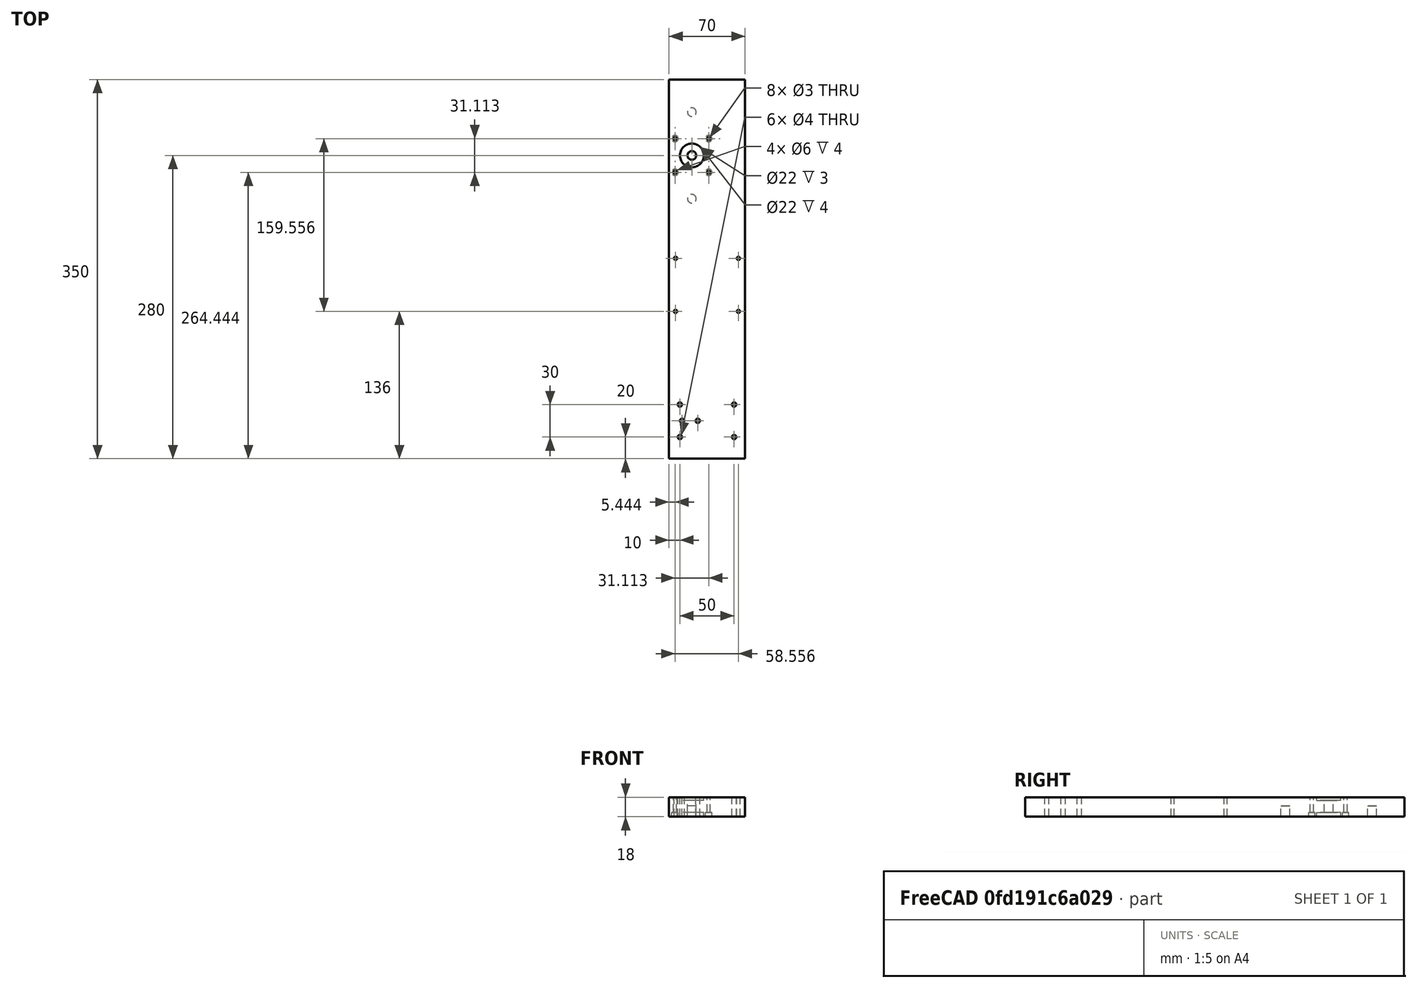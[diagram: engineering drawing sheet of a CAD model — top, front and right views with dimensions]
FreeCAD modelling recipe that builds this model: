
FCSTD DOCUMENT  (FreeCAD 0.17R13541 (Git))
Label: X-Izquierda
License: All rights reserved
LicenseURL: http://en.wikipedia.org/wiki/All_rights_reserved
objects: Part::Cylinder×16, Part::Cut×6, Part::MultiFuse×3, Part::FeaturePython×3, Part::Box×1
note: 29 computed .brp shape members not serialized (recipe doc carries the construction recipe); baked Part::Feature solids carry a one-line shape summary decoded from their .brp

FEATURE [Part::Box] Box  label="Base"
  AttacherType = Attacher::AttachEngine3D
  Height = 18
  Length = 70
  Width = 350
FEATURE [Part::Cylinder] Cylinder  label="Cilindro"
  Angle = 360
  AttacherType = Attacher::AttachEngine3D
  Height = 25
  Placement = pos=(10,20,0) rot=(0,0,1;0rad)
  Radius = 2
FEATURE [Part::Cylinder] Cylinder001  label="Cilindro001"
  Angle = 360
  AttacherType = Attacher::AttachEngine3D
  Height = 25
  Placement = pos=(60,20,0) rot=(0,0,1;0rad)
  Radius = 2
FEATURE [Part::Cylinder] Cylinder002  label="Cilindro002"
  Angle = 360
  AttacherType = Attacher::AttachEngine3D
  Height = 25
  Placement = pos=(10,50,0) rot=(0,0,1;0rad)
  Radius = 2
FEATURE [Part::Cylinder] Cylinder003  label="Cilindro003"
  Angle = 360
  AttacherType = Attacher::AttachEngine3D
  Height = 25
  Placement = pos=(60,50,0) rot=(0,0,1;0rad)
  Radius = 2
FEATURE [Part::Cylinder] Cylinder004  label="Cilindro004"
  Angle = 360
  AttacherType = Attacher::AttachEngine3D
  Height = 25
  Placement = pos=(12,35,0) rot=(0,0,1;0rad)
  Radius = 2
FEATURE [Part::Cylinder] Cylinder005  label="Cilindro005"
  Angle = 360
  AttacherType = Attacher::AttachEngine3D
  Height = 25
  Placement = pos=(26.5,35,0) rot=(0,0,1;0rad)
  Radius = 2
FEATURE [Part::MultiFuse] Fusion
  Refine = true
  Shapes = -> [Cylinder005,Cylinder003,Cylinder004,Cylinder002,Cylinder001,Cylinder]
FEATURE [Part::Cylinder] Cylinder006  label="Cilindro006"
  Angle = 360
  AttacherType = Attacher::AttachEngine3D
  Height = 25
  Placement = pos=(64,136,0) rot=(0,0,1;0rad)
  Radius = 1.5
FEATURE [Part::Cylinder] Cylinder007  label="Cilindro007"
  Angle = 360
  AttacherType = Attacher::AttachEngine3D
  Height = 25
  Placement = pos=(6,136,0) rot=(0,0,1;0rad)
  Radius = 1.5
FEATURE [Part::Cylinder] Cylinder008  label="Cilindro008"
  Angle = 360
  AttacherType = Attacher::AttachEngine3D
  Height = 25
  Placement = pos=(6,185,0) rot=(0,0,1;0rad)
  Radius = 1.5
FEATURE [Part::Cylinder] Cylinder009  label="Cilindro009"
  Angle = 360
  AttacherType = Attacher::AttachEngine3D
  Height = 25
  Placement = pos=(64,185,0) rot=(0,0,1;0rad)
  Radius = 1.5
FEATURE [Part::Cut] Cut
  Base = -> Box
  Refine = true
  Tool = -> Fusion
FEATURE [Part::MultiFuse] Fusion001
  Refine = true
  Shapes = -> [Cylinder009,Cylinder008,Cylinder007,Cylinder006]
FEATURE [Part::Cut] Cut001
  Base = -> Cut
  Refine = true
  Tool = -> Fusion001
FEATURE [Part::Cylinder] Cylinder010  label="Cilindro010"
  Angle = 360
  AttacherType = Attacher::AttachEngine3D
  Height = 25
  Placement = pos=(22,0,0) rot=(0,0,1;0rad)
  Radius = 1.5
FEATURE [Part::FeaturePython] Array  # Draft array (typed FeaturePython)
  Angle = 360
  ArrayType = 1
  Axis = (0,0,1)
  Base = -> Cylinder010
  Center = (0,0,0)
  Fuse = false
  IntervalAxis = (0,0,0)
  IntervalX = (1,0,0)
  IntervalY = (0,1,0)
  IntervalZ = (0,0,0)
  NumberPolar = 4
  NumberX = 2
  NumberY = 2
  NumberZ = 1
  Placement = pos=(21,280,0) rot=(0,0,1;0.785398rad)
FEATURE [Part::Cylinder] Cylinder011  label="Cilindro011"
  Angle = 360
  AttacherType = Attacher::AttachEngine3D
  Height = 25
  Radius = 4
FEATURE [Part::Cylinder] Cylinder012  label="Cilindro012"
  Angle = 360
  AttacherType = Attacher::AttachEngine3D
  Height = 10
  Placement = pos=(0,0,15) rot=(0,0,1;0rad)
  Radius = 11
FEATURE [Part::Cylinder] Cylinder013  label="Cilindro013"
  Angle = 360
  AttacherType = Attacher::AttachEngine3D
  Height = 4
  Radius = 11
FEATURE [Part::MultiFuse] Fusion002
  Placement = pos=(21,280,0) rot=(0,0,1;0rad)
  Refine = true
  Shapes = -> [Cylinder013,Cylinder011,Cylinder012]
FEATURE [Part::Cut] Cut002
  Base = -> Cut001
  Refine = true
  Tool = -> Array
FEATURE [Part::Cut] Cut003
  Base = -> Cut002
  Refine = true
  Tool = -> Fusion002
FEATURE [Part::Cylinder] Cylinder014  label="Cilindro014"
  Angle = 360
  AttacherType = Attacher::AttachEngine3D
  Height = 10
  Radius = 4
FEATURE [Part::FeaturePython] Array001  # Draft array (typed FeaturePython)
  Angle = 360
  ArrayType = 0
  Axis = (0,0,1)
  Base = -> Cylinder014
  Center = (0,0,0)
  Fuse = false
  IntervalAxis = (0,0,0)
  IntervalX = (0,0,0)
  IntervalY = (0,80,0)
  IntervalZ = (0,0,0)
  NumberPolar = 1
  NumberX = 1
  NumberY = 2
  NumberZ = 1
  Placement = pos=(21,240,0) rot=(0,0,1;0rad)
FEATURE [Part::Cut] Cut004
  Base = -> Cut003
  Refine = true
  Tool = -> Array001
FEATURE [Part::Cylinder] Cylinder015  label="Cilindro015"
  Angle = 360
  AttacherType = Attacher::AttachEngine3D
  Height = 4
  Placement = pos=(22,0,0) rot=(0,0,1;0rad)
  Radius = 3
FEATURE [Part::FeaturePython] Array002  # Draft array (typed FeaturePython)
  Angle = 360
  ArrayType = 1
  Axis = (0,0,1)
  Base = -> Cylinder015
  Center = (0,0,0)
  Fuse = false
  IntervalAxis = (0,0,0)
  IntervalX = (1,0,0)
  IntervalY = (0,1,0)
  IntervalZ = (0,0,0)
  NumberPolar = 4
  NumberX = 2
  NumberY = 2
  NumberZ = 1
  Placement = pos=(21,280,0) rot=(0,0,1;0.785398rad)
FEATURE [Part::Cut] Cut005
  Base = -> Cut004
  Refine = true
  Tool = -> Array002
